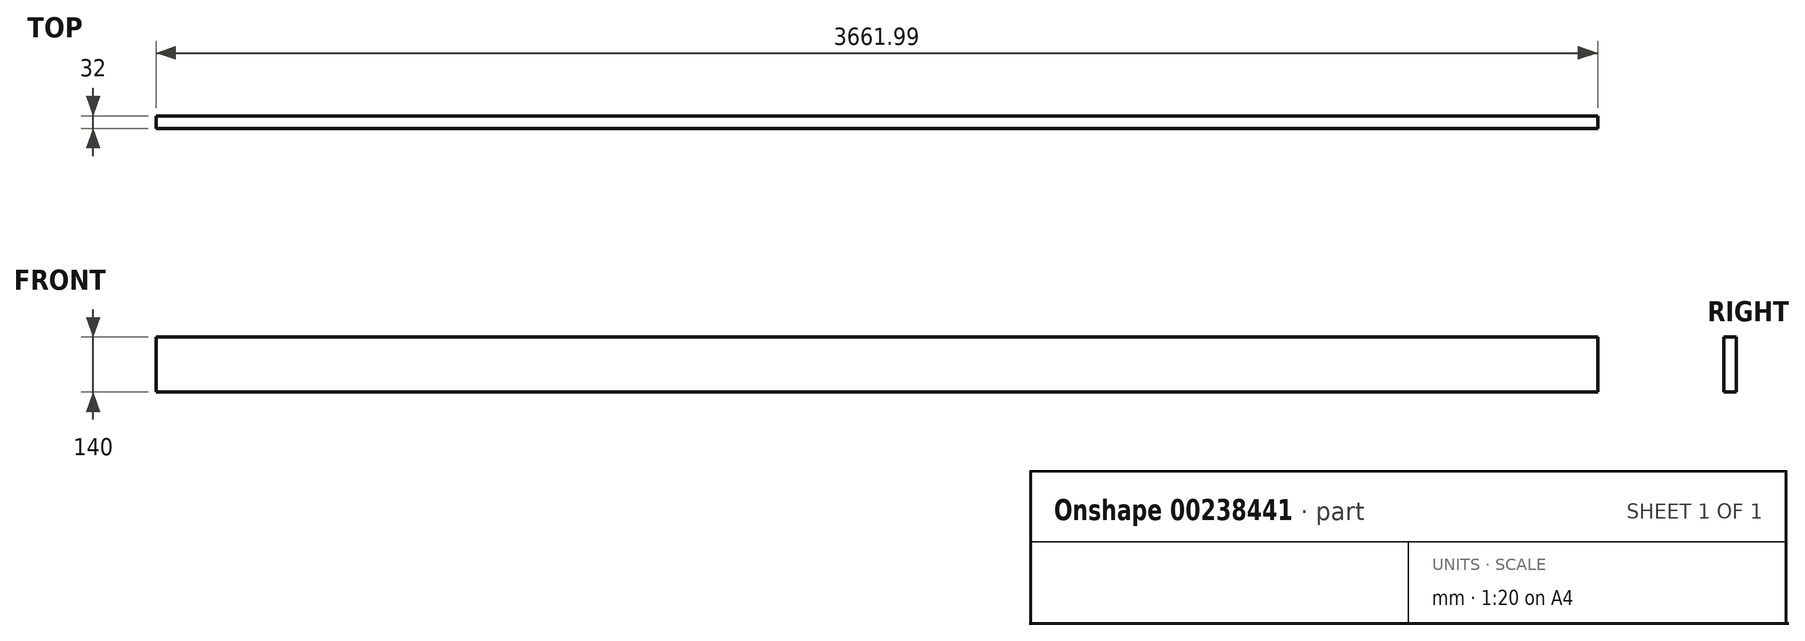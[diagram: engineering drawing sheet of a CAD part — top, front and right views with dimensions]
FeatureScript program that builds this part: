
annotation { "Feature Type Name" : "Feature", "Feature Type Description" : "" }
export const myFeature = defineFeature(function(context is Context, id is Id, definition is map)
    precondition{}
    {
        {
            var Q0;
            Q0=qCreatedBy(makeId("Front.planeOp"),FACE);
            var sketch = newSketch(context, id + "F0", { "sketchPlane" : qUnion([Q0])});
            skLineSegment(sketch, "E0.bottom", {"start": v(-4640.6, -2644.52) * mm, "end": v(-978.6, -2644.52) * mm});
            skLineSegment(sketch, "E0.top", {"start": v(-4640.6, -2504.52) * mm, "end": v(-978.6, -2504.52) * mm});
            skLineSegment(sketch, "E0.left", {"start": v(-4640.6, -2644.52) * mm, "end": v(-4640.6, -2504.52) * mm});
            skLineSegment(sketch, "E0.right", {"start": v(-978.6, -2644.52) * mm, "end": v(-978.6, -2504.52) * mm});
            skSolve(sketch);
        }
        {
            var Q0;
            Q0=makeQuery(id+"F0.imprint","IMPRINT",FACE,{"disambiguationData":[TD([[makeQuery(id+"F0.imprint","IMPRINT",EDGE,{"derivedFrom":sQuery(id+"F0.wireOp",EDGE,"E0.bottom")}),1.0]])]});
            extrude(context, id + "F1", {"entities" : qUnion([Q0]), "depth" : 32 * mm});
        }
    });
